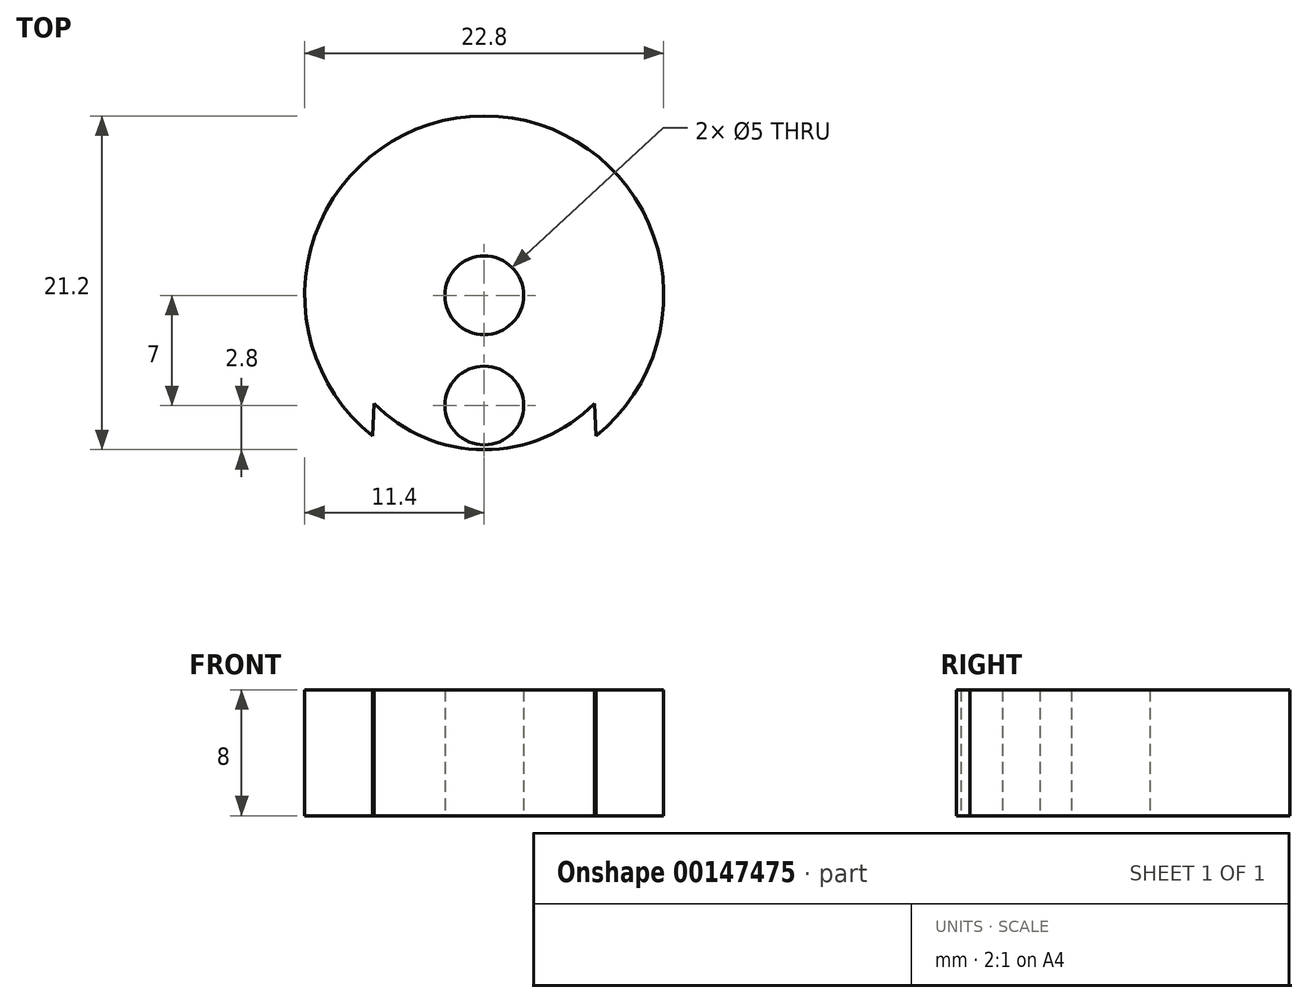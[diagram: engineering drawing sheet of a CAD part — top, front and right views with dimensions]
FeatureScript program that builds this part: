
annotation { "Feature Type Name" : "Feature", "Feature Type Description" : "" }
export const myFeature = defineFeature(function(context is Context, id is Id, definition is map)
    precondition{}
    {
        {
            var Q0;
            Q0=qCreatedBy(makeId("Top.planeOp"),FACE);
            var sketch = newSketch(context, id + "F0", { "sketchPlane" : qUnion([Q0])});
            skCircle(sketch, "E0", {"center": v(0, 0) * mm, "radius": 11.4 * mm});
            skCircle(sketch, "E1", {"center": v(0, 0) * mm, "radius": 9.8 * mm});
            skCircle(sketch, "E2", {"center": v(0, 0) * mm, "radius": 4.25 * mm});
            skCircle(sketch, "E3", {"center": v(0, 0) * mm, "radius": 2.5 * mm});
            skCircle(sketch, "E4", {"center": v(0, -7) * mm, "radius": 2.5 * mm});
            skCircle(sketch, "E5", {"center": v(0, 0) * mm, "radius": 7 * mm, "construction": true});
            skLineSegment(sketch, "E6", {"start": v(-7, -6.86) * mm, "end": v(-7.1, -8.92) * mm});
            skLineSegment(sketch, "E7.MirrorCS", {"start": v(7, -6.86) * mm, "end": v(7.1, -8.92) * mm});
            skSolve(sketch);
        }
        {
            var Q0;
            Q0=makeQuery(id+"F0.imprint","IMPRINT",FACE,{"disambiguationData":[TD([[makeQuery(id+"F0.imprint","IMPRINT",EDGE,{"derivedFrom":sQuery(id+"F0.wireOp",EDGE,"E2")}),1.0]])]});
            extrude(context, id + "F1", {"entities" : qUnion([Q0]), "depth" : 8 * mm});
        }
        {
            var Q0;
            Q0=makeQuery(id+"F0.imprint","IMPRINT",FACE,{"disambiguationData":[TD([[makeQuery(id+"F0.imprint","IMPRINT",EDGE,{"derivedFrom":sQuery(id+"F0.wireOp",EDGE,"E1")}),1.0]])]});
            var Q1;
            {var subQ0=sQuery(id+"F0.wireOp",EDGE,"E6");Q1=makeQuery(id+"F0.imprint","IMPRINT",FACE,{"disambiguationData":[TD([[makeQuery(id+"F0.imprint","IMPRINT",EDGE,{"derivedFrom":subQ0}),-1.0]])]});}
            extrude(context, id + "F2", {"entities" : qUnion([Q0, Q1]), "operationType" : NewBodyOperationType.ADD, "depth" : 8 * mm});
        }
    });
